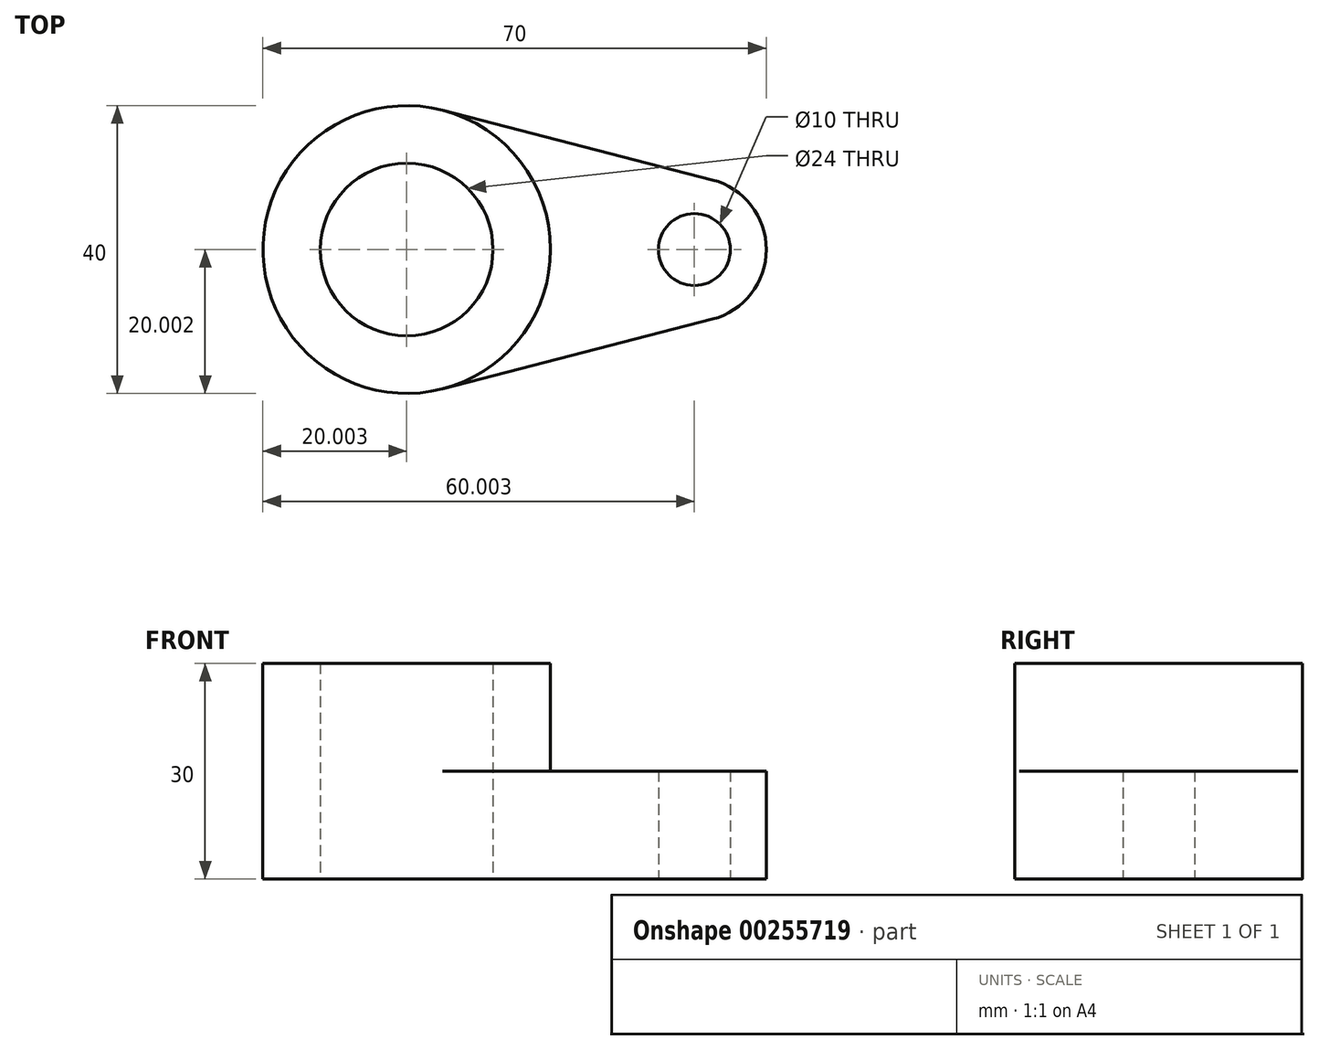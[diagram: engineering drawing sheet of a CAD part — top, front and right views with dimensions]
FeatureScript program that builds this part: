
annotation { "Feature Type Name" : "Feature", "Feature Type Description" : "" }
export const myFeature = defineFeature(function(context is Context, id is Id, definition is map)
    precondition{}
    {
        {
            var Q0;
            Q0=qCreatedBy(makeId("Top.planeOp"),FACE);
            var sketch = newSketch(context, id + "F0", { "sketchPlane" : qUnion([Q0])});
            skCircle(sketch, "E0", {"center": v(-61.96, 21.61) * mm, "radius": 12 * mm});
            skCircle(sketch, "E1", {"center": v(-61.96, 21.61) * mm, "radius": 20 * mm});
            skCircle(sketch, "E2", {"center": v(-21.96, 21.61) * mm, "radius": 5 * mm});
            skArc(sketch, "E3", {"start": v(-19.46, 11.93) * mm, "mid": v(-11.96, 21.61) * mm, "end": v(-19.46, 31.3) * mm});
            skLineSegment(sketch, "E4", {"start": v(-56.96, 40.98) * mm, "end": v(-19.46, 31.3) * mm});
            skLineSegment(sketch, "E5", {"start": v(-56.96, 2.25) * mm, "end": v(-19.46, 11.93) * mm});
            skSolve(sketch);
        }
        {
            var Q0;
            Q0=makeQuery(id+"F0.imprint","IMPRINT",FACE,{"disambiguationData":[TD([[makeQuery(id+"F0.imprint","IMPRINT",EDGE,{"derivedFrom":sQuery(id+"F0.wireOp",EDGE,"E2")}),-1.0]])]});
            extrude(context, id + "F1", {"entities" : qUnion([Q0]), "depth" : 15 * mm});
        }
        {
            var Q0;
            Q0=makeQuery(id+"F0.imprint","IMPRINT",FACE,{"disambiguationData":[TD([[makeQuery(id+"F0.imprint","IMPRINT",EDGE,{"derivedFrom":sQuery(id+"F0.wireOp",EDGE,"E2")}),-1.0]])]});
            extrude(context, id + "F2", {"entities" : qUnion([Q0]), "operationType" : NewBodyOperationType.ADD, "depth" : 15 * mm});
        }
        {
            var Q0;
            Q0=makeQuery(id+"F0.imprint","IMPRINT",FACE,{"disambiguationData":[TD([[makeQuery(id+"F0.imprint","IMPRINT",EDGE,{"derivedFrom":sQuery(id+"F0.wireOp",EDGE,"E0")}),-1.0]])]});
            extrude(context, id + "F3", {"entities" : qUnion([Q0]), "operationType" : NewBodyOperationType.ADD, "depth" : 30 * mm});
        }
    });
